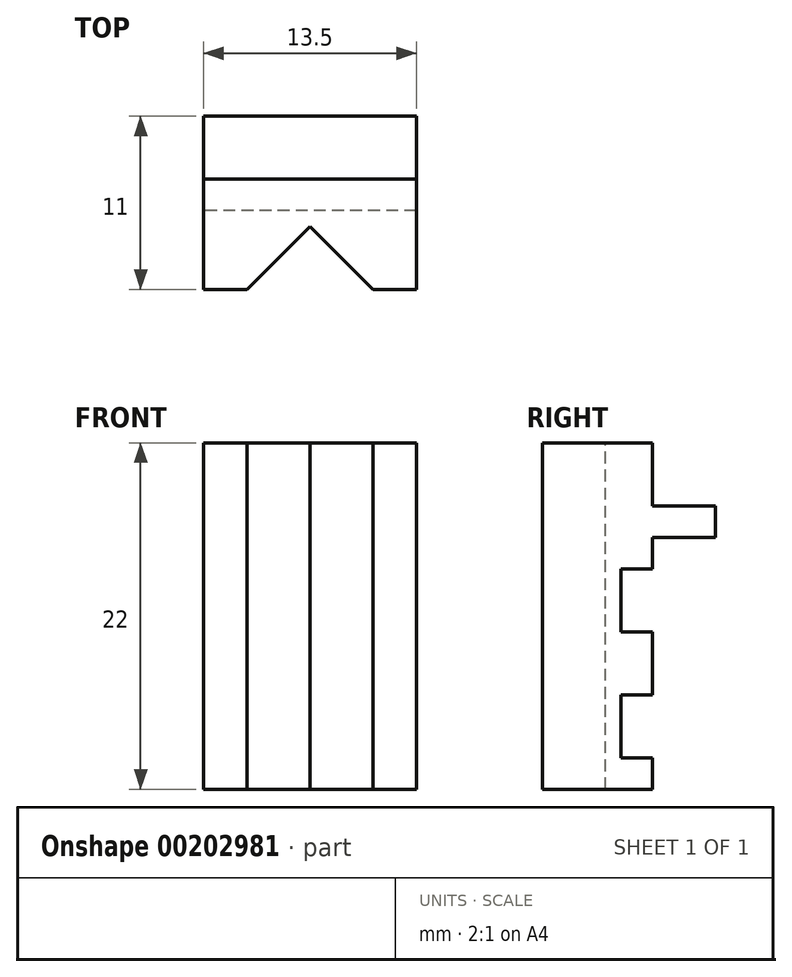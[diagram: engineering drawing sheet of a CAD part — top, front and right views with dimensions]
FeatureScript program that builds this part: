
annotation { "Feature Type Name" : "Feature", "Feature Type Description" : "" }
export const myFeature = defineFeature(function(context is Context, id is Id, definition is map)
    precondition{}
    {
        {
            var Q0;
            Q0=qCreatedBy(makeId("Front.planeOp"),FACE);
            var sketch = newSketch(context, id + "F0", { "sketchPlane" : qUnion([Q0])});
            skLineSegment(sketch, "E0.bottom", {"start": v(6.75, -9) * mm, "end": v(-6.75, -9) * mm, "construction": true});
            skLineSegment(sketch, "E0.top", {"start": v(6.75, 9) * mm, "end": v(-6.75, 9) * mm, "construction": true});
            skLineSegment(sketch, "E0.left", {"start": v(6.75, -9) * mm, "end": v(6.75, 9) * mm});
            skLineSegment(sketch, "E0.right", {"start": v(-6.75, -9) * mm, "end": v(-6.75, 9) * mm});
            skPoint(sketch, "E0.middle", {"position": v(0, 0) * mm});
            skLineSegment(sketch, "E1", {"start": v(-6.75, 9) * mm, "end": v(-6.75, 11) * mm});
            skLineSegment(sketch, "E2", {"start": v(-6.75, 11) * mm, "end": v(6.75, 11) * mm});
            skLineSegment(sketch, "E3", {"start": v(6.75, 11) * mm, "end": v(6.75, 9) * mm});
            skLineSegment(sketch, "E4", {"start": v(-6.75, -9) * mm, "end": v(-6.75, -11) * mm});
            skLineSegment(sketch, "E5", {"start": v(-6.75, -11) * mm, "end": v(6.75, -11) * mm});
            skLineSegment(sketch, "E6", {"start": v(6.75, -11) * mm, "end": v(6.75, -9) * mm});
            skSolve(sketch);
        }
        {
            var Q0;
            Q0 = qSketchRegion(id + "F0", true);
            extrude(context, id + "F1", {"entities" : qUnion([Q0]), "depth" : 7 * mm});
        }
        {
            var Q0;
            Q0=makeQuery(id+"F1.opExtrude","CAP_FACE",FACE,{"disambiguationData":[OSD([sQuery(id+"F0.wireOp",EDGE,"E0.left"),sQuery(id+"F0.wireOp",EDGE,"E0.right"),sQuery(id+"F0.wireOp",EDGE,"E1"),sQuery(id+"F0.wireOp",EDGE,"E2"),sQuery(id+"F0.wireOp",EDGE,"E3"),sQuery(id+"F0.wireOp",EDGE,"E4"),sQuery(id+"F0.wireOp",EDGE,"E5"),sQuery(id+"F0.wireOp",EDGE,"E6")])],"isStart":true});
            var sketch = newSketch(context, id + "F2", { "sketchPlane" : qUnion([Q0])});
            skLineSegment(sketch, "E7.bottom", {"start": v(-6.75, 7) * mm, "end": v(6.75, 7) * mm});
            skLineSegment(sketch, "E7.top", {"start": v(-6.75, 5) * mm, "end": v(6.75, 5) * mm});
            skLineSegment(sketch, "E7.left", {"start": v(-6.75, 7) * mm, "end": v(-6.75, 5) * mm});
            skLineSegment(sketch, "E7.right", {"start": v(6.75, 7) * mm, "end": v(6.75, 5) * mm});
            skSolve(sketch);
        }
        {
            var Q0;
            Q0 = qSketchRegion(id + "F2", true);
            extrude(context, id + "F3", {"entities" : qUnion([Q0]), "operationType" : NewBodyOperationType.ADD, "depth" : 4 * mm});
        }
        {
            var Q0;
            Q0=makeQuery(id+"F1.opExtrude","SWEPT_FACE",FACE,{"disambiguationData":[OSD([sQuery(id+"F0.wireOp",EDGE,"E2")])]});
            var sketch = newSketch(context, id + "F4", { "sketchPlane" : qUnion([Q0])});
            skLineSegment(sketch, "E8", {"start": v(0, -3) * mm, "end": v(-4, -7) * mm});
            skLineSegment(sketch, "E9", {"start": v(-4, -7) * mm, "end": v(4, -7) * mm});
            skLineSegment(sketch, "E10", {"start": v(4, -7) * mm, "end": v(0, -3) * mm});
            skSolve(sketch);
        }
        {
            var Q0;
            Q0 = qSketchRegion(id + "F4", true);
            var Q1;
            Q1=makeQuery(id+"F1.opExtrude","SWEPT_FACE",FACE,{"disambiguationData":[OSD([sQuery(id+"F0.wireOp",EDGE,"E5")])]});
            extrude(context, id + "F5", {"entities" : qUnion([Q0]), "operationType" : NewBodyOperationType.REMOVE, "endBound" : BoundingType.UP_TO_SURFACE, "oppositeDirection" : true, "endBoundEntityFace" : qUnion([Q1]), "depth" : 25 * mm});
        }
        {
            var Q0;
            {var subQ0=sQuery(id+"F0.wireOp",EDGE,"E5");var subQ1=sQuery(id+"F0.wireOp",EDGE,"E4");var subQ2=sQuery(id+"F0.wireOp",EDGE,"E1");var subQ3=sQuery(id+"F0.wireOp",EDGE,"E0.right");var subQ4=sQuery(id+"F0.wireOp",EDGE,"E6");var subQ5=sQuery(id+"F0.wireOp",EDGE,"E3");var subQ6=sQuery(id+"F0.wireOp",EDGE,"E0.left");Q0=makeQuery(id+"F3.boolean.opBoolean","SPLIT",FACE,{"disambiguationData":[TD([makeQuery(id+"F1.opExtrude","SWEPT_FACE",FACE,{"disambiguationData":[OSD([subQ0])]})])],"derivedFrom":makeQuery(id+"F1.opExtrude","CAP_FACE",FACE,{"disambiguationData":[OSD([subQ6,subQ3,subQ2,sQuery(id+"F0.wireOp",EDGE,"E2"),subQ5,subQ1,subQ0,subQ4])],"isStart":true})});}
            var sketch = newSketch(context, id + "F6", { "sketchPlane" : qUnion([Q0])});
            skLineSegment(sketch, "E11.bottom", {"start": v(-6.75, 3) * mm, "end": v(6.75, 3) * mm});
            skLineSegment(sketch, "E11.top", {"start": v(-6.75, -1) * mm, "end": v(6.75, -1) * mm});
            skLineSegment(sketch, "E11.left", {"start": v(-6.75, 3) * mm, "end": v(-6.75, -1) * mm});
            skLineSegment(sketch, "E11.right", {"start": v(6.75, 3) * mm, "end": v(6.75, -1) * mm});
            skLineSegment(sketch, "E12.bottom", {"start": v(-6.75, -5) * mm, "end": v(6.75, -5) * mm});
            skLineSegment(sketch, "E12.top", {"start": v(-6.75, -9) * mm, "end": v(6.75, -9) * mm});
            skLineSegment(sketch, "E12.left", {"start": v(-6.75, -5) * mm, "end": v(-6.75, -9) * mm});
            skLineSegment(sketch, "E12.right", {"start": v(6.75, -5) * mm, "end": v(6.75, -9) * mm});
            skSolve(sketch);
        }
        {
            var Q0;
            Q0 = qSketchRegion(id + "F6", true);
            extrude(context, id + "F7", {"entities" : qUnion([Q0]), "operationType" : NewBodyOperationType.REMOVE, "oppositeDirection" : true, "depth" : 2 * mm});
        }
    });
